# Revit family: WCSeat-Vitra-SentoSeries_130
name_source: partatom
category: Plumbing Fixtures
revit_build: Autodesk Revit 2017 (Build: 20160225_1515(x64)
units: mm (PartAtom-declared; Revit-internal decimal feet)

## family parameters
Cut with Voids When Loaded = No
Host = Face
OmniClass Number = 23.45.05.21.11
OmniClass Title = Water Closets
Part Type = Normal
Room Calculation Point = No
Round Connector Dimension = Use Diameter
Shared = Yes

## types (6) — shared parameters
BIMobject category = Sanitary - Toilet Seats
Brand = VitrA
CW Connection = No
Default Elevation = 410 mm  [stored 1.34514 ft]
Design country = Turkey
HW Connection = No
IFC Classification = Sanitary Terminal
Main Material = Plastic
Manufacturer = VitrA
Manufacturer name = VitrA
Mounting type = Face
NBS Referans Code = 35-93-95
NBS Referans Description = Wc Seats And Covers
Nominal Depth (mm) = 452 mm  [stored 1.48294 ft]
Nominal Height (mm) = 50 mm  [stored 0.164042 ft]
Nominal Width (mm) = 367 mm  [stored 1.20407 ft]
OmniClass Code = 23-31 19 19 11
OmniClass Description = Toilets
Product certification = https://www.vitraglobal.com
Product data url = https://www.vitra-bad.de
Product family = Sento
Secondary Material = Metal
Technical description = https://www.vitra-bad.de
UNSPSC Code = 35-93-95
UNSPSC Description = Water Operated Water Closets
URL = https://www.vitraglobal.com
Uniclass 1.4 Code = L72164
Uniclass 1.4 Description = Toilets
Uniclass 2.0 Code = PR-35-93-95
Uniclass 2.0 Description = Wc Seats And Covers
Uniclass 2015 Code = Pr_40_20_93_95
Uniclass 2015 Name = WC seats and covers
Vent Connection = No
Warranty Period (Year) = 2 Years
Waste Connection = No
Weight Net (kg) = 3
Youtube = https://www.youtube.com

## per-type parameters (varying)
| type | Article No. (default) | Color | Description | Model | Primary Material | Product SKU |
| WCSeat-MetalHinge-TopFixing-QuickRelease-White-Vitra_Sento_130-003R409 | 130-003R409 | White | VitrA Sento  WC Seat - Metal Hinge - Top Fixing - Quick Release | 130-003R409 | White-WCSeat | 130-003R409 |
| WCSeat-MetalHinge-TopFixing-SoftClosing-MatteWhite-Vitra_Sento_130-001R409 | 130-001R409 | MatteWhite | VitrA Sento  WC Seat - Metal Hinge - Top Fixing - Soft Closing | 130-001R409 | MatteWhite-WCSeat | 130-001R409 |
| WCSeat-MetalHinge-TopFixing-SoftClosing-MatteTaupe-Vitra_Sento_130-020R409 | 130-020R409 | Matte Taupe | VitrA Sento  WC Seat - Metal Hinge - Top Fixing - Soft Closing | 130-020R409 | MatteTaupe-WCSeat | 130-020R409 |
| WCSeat-MetalHinge-TopFixing-SoftClosing-MatteMink-Vitra_Sento_130-050R409 | 130-050R409 | Matte Mink | VitrA Sento  WC Seat - Metal Hinge - Top Fixing - Soft Closing | 130-050R409 | MatteMink-WCSeat | 130-050R409 |
| WCSeat-MetalHinge-TopFixing-SoftClosing-MatteBlack-Vitra_Sento_130-083R409 | 130-083R409 | Matte Black | VitrA Sento  WC Seat - Metal Hinge - Top Fixing - Soft Closing | 130-083R409 | MatteBlack-WCSeat | 130-083R409 |
| WCSeat-MetalHinge-TopFixing-SoftClosing-HighglossBlack-Vitra_Sento_130-070R409 | 130-070R409 | High gloss Black | VitrA Sento  WC Seat - Metal Hinge - Top Fixing - Soft Closing | 130-070R409 | HighGlossBlack-WCSeat | 130-070R409 |

note: [stored X ft] marks values corroborated as IEEE doubles in the binary element streams (Revit-internal decimal feet)

## geometry (parser evidence)
native form markers: Sweep x2
no freeform markers — native parametric forms only
